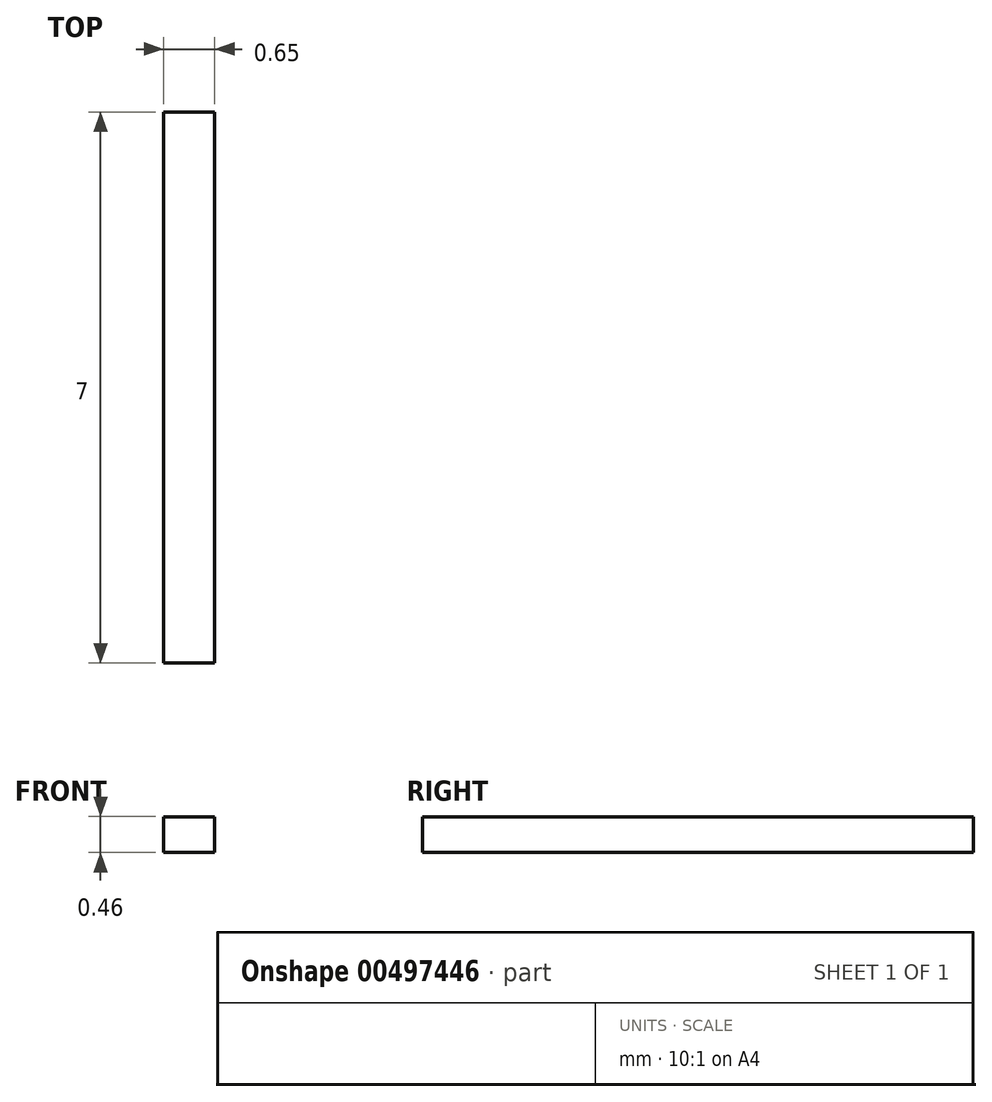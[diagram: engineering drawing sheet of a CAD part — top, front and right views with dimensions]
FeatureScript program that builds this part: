
annotation { "Feature Type Name" : "Feature", "Feature Type Description" : "" }
export const myFeature = defineFeature(function(context is Context, id is Id, definition is map)
    precondition{}
    {
        {
            var Q0;
            Q0=qCreatedBy(makeId("Front.planeOp"),FACE);
            var sketch = newSketch(context, id + "F0", { "sketchPlane" : qUnion([Q0])});
            skLineSegment(sketch, "E0", {"start": v(0, 0) * mm, "end": v(0.65, 0) * mm});
            skLineSegment(sketch, "E1", {"start": v(0.65, 0) * mm, "end": v(0.65, 0.46) * mm});
            skLineSegment(sketch, "E2", {"start": v(0.65, 0.46) * mm, "end": v(0, 0.46) * mm});
            skLineSegment(sketch, "E3", {"start": v(0, 0.46) * mm, "end": v(0, 0) * mm});
            skSolve(sketch);
        }
        {
            var Q0;
            Q0 = qSketchRegion(id + "F0", true);
            extrude(context, id + "F1", {"entities" : qUnion([Q0]), "depth" : 7 * mm});
        }
    });
